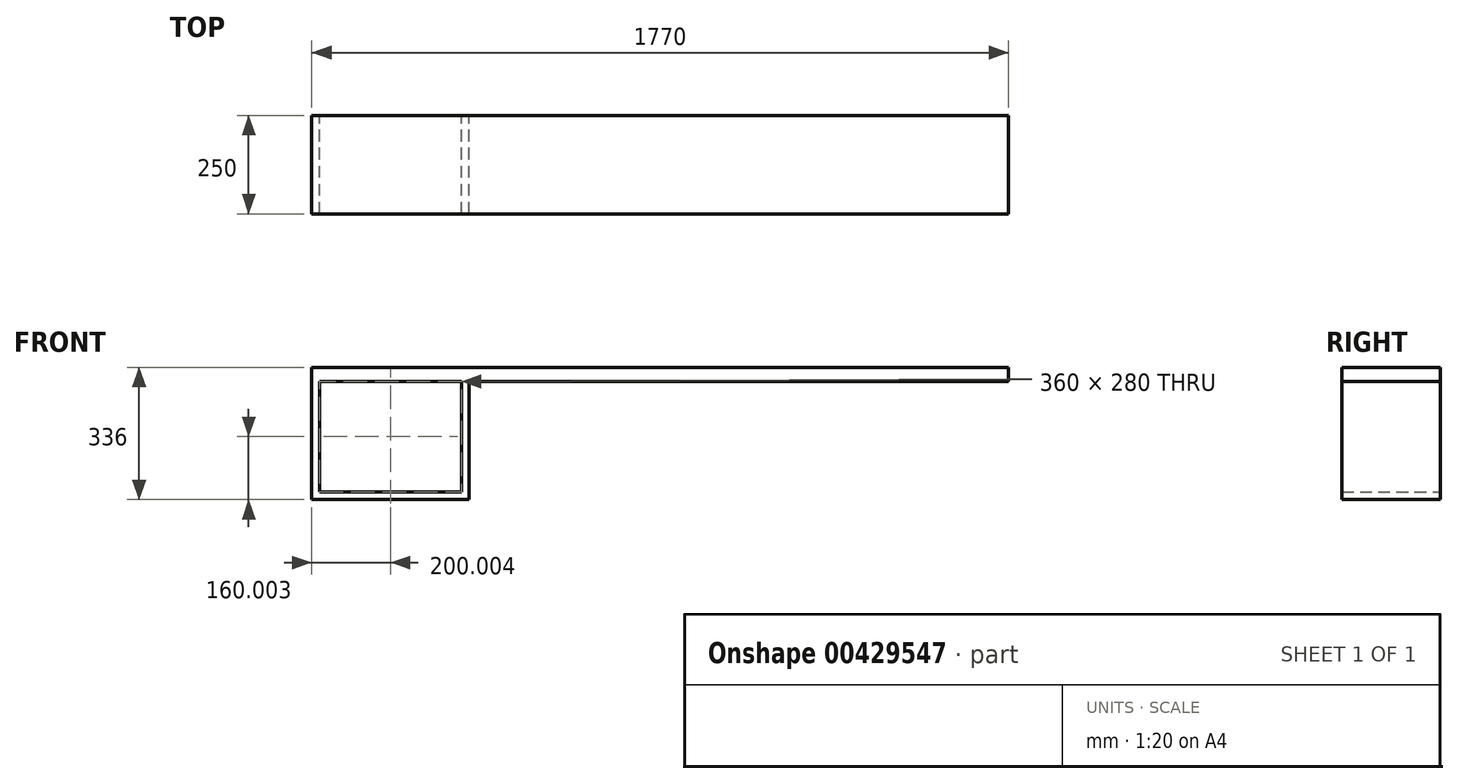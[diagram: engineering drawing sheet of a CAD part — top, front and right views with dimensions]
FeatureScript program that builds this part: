
annotation { "Feature Type Name" : "Feature", "Feature Type Description" : "" }
export const myFeature = defineFeature(function(context is Context, id is Id, definition is map)
    precondition{}
    {
        {
            var Q0;
            Q0=qCreatedBy(makeId("Front.planeOp"),FACE);
            var sketch = newSketch(context, id + "F0", { "sketchPlane" : qUnion([Q0])});
            skLineSegment(sketch, "E0.top", {"start": v(1486.02, 125.11) * mm, "end": v(-283.98, 125.11) * mm});
            skLineSegment(sketch, "E0.left", {"start": v(1486.02, 89.11) * mm, "end": v(1486.02, 125.11) * mm});
            skLineSegment(sketch, "E0.right", {"start": v(-283.98, -60.89) * mm, "end": v(-283.98, 125.11) * mm});
            skPoint(sketch, "E0.middle", {"position": v(601.02, 0.11) * mm});
            skLineSegment(sketch, "E1.0", {"start": v(1486.02, 89.11) * mm, "end": v(-283.98, 89.11) * mm});
            skLineSegment(sketch, "E2.0", {"start": v(116.02, -60.89) * mm, "end": v(116.02, 125.11) * mm});
            skLineSegment(sketch, "E3.0", {"start": v(116.02, -60.89) * mm, "end": v(-283.98, -60.89) * mm});
            skLineSegment(sketch, "E4.0", {"start": v(116.02, -210.89) * mm, "end": v(-283.98, -210.89) * mm});
            skPoint(sketch, "E5.orphan", {"position": v(1486.02, -124.89) * mm});
            skPoint(sketch, "E6.orphan", {"position": v(-283.98, -124.89) * mm});
            skLineSegment(sketch, "E7", {"start": v(116.02, -60.89) * mm, "end": v(116.02, -210.89) * mm});
            skLineSegment(sketch, "E8", {"start": v(-283.98, -60.89) * mm, "end": v(-283.98, -210.89) * mm});
            skLineSegment(sketch, "E9.0", {"start": v(96.02, -60.89) * mm, "end": v(96.02, 125.11) * mm});
            skLineSegment(sketch, "E9.1", {"start": v(96.02, -60.89) * mm, "end": v(96.02, -210.89) * mm});
            skLineSegment(sketch, "E10.0", {"start": v(116.02, -190.89) * mm, "end": v(-283.98, -190.89) * mm});
            skLineSegment(sketch, "E11.0", {"start": v(-263.98, -60.89) * mm, "end": v(-263.98, -210.89) * mm});
            skLineSegment(sketch, "E12.0", {"start": v(-263.98, -60.89) * mm, "end": v(-263.98, 125.11) * mm});
            skSolve(sketch);
        }
        {
            var Q0;
            {var subQ0=sQuery(id+"F0.wireOp",EDGE,"E0.left");Q0=makeQuery(id+"F0.imprint","IMPRINT",FACE,{"disambiguationData":[TD([[makeQuery(id+"F0.imprint","IMPRINT",EDGE,{"derivedFrom":subQ0}),1.0]])]});}
            var Q1;
            {var subQ0=sQuery(id+"F0.wireOp",EDGE,"E0.right");var subQ1=sQuery(id+"F0.wireOp",EDGE,"E0.top");var subQ2=makeQuery(id+"F0.imprint","INTERSECT",VERTEX,{"derivedFrom":[subQ1,subQ0]});Q1=makeQuery(id+"F0.imprint","IMPRINT",FACE,{"disambiguationData":[TD([[makeQuery(id+"F0.imprint","IMPRINT",EDGE,{"disambiguationData":[TD([[subQ2,1.0]])],"derivedFrom":subQ1}),1.0]])]});}
            var Q2;
            {var subQ0=sQuery(id+"F0.wireOp",EDGE,"E9.0");var subQ1=sQuery(id+"F0.wireOp",EDGE,"E0.top");var subQ2=makeQuery(id+"F0.imprint","INTERSECT",VERTEX,{"derivedFrom":[subQ1,subQ0]});Q2=makeQuery(id+"F0.imprint","IMPRINT",FACE,{"disambiguationData":[TD([[makeQuery(id+"F0.imprint","IMPRINT",EDGE,{"disambiguationData":[TD([[subQ2,-1.0]])],"derivedFrom":subQ1}),1.0]])]});}
            var Q3;
            {var subQ0=sQuery(id+"F0.wireOp",EDGE,"E2.0");var subQ1=sQuery(id+"F0.wireOp",EDGE,"E0.top");var subQ2=makeQuery(id+"F0.imprint","INTERSECT",VERTEX,{"derivedFrom":[subQ1,subQ0]});Q3=makeQuery(id+"F0.imprint","IMPRINT",FACE,{"disambiguationData":[TD([[makeQuery(id+"F0.imprint","IMPRINT",EDGE,{"disambiguationData":[TD([[subQ2,-1.0]])],"derivedFrom":subQ1}),1.0]])]});}
            extrude(context, id + "F1", {"entities" : qUnion([Q0, Q1, Q2, Q3]), "depth" : 250 * mm});
        }
        {
            var Q0;
            {var subQ1=sQuery(id+"F0.wireOp",EDGE,"E0.right");var subQ3=sQuery(id+"F0.wireOp",EDGE,"E1.0");var subQ4=makeQuery(id+"F0.imprint","INTERSECT",VERTEX,{"derivedFrom":[subQ1,subQ3]});Q0=makeQuery(id+"F0.imprint","IMPRINT",FACE,{"disambiguationData":[TD([[makeQuery(id+"F0.imprint","IMPRINT",EDGE,{"disambiguationData":[TD([[subQ4,1.0]])],"derivedFrom":subQ3}),1.0]])]});}
            var Q1;
            {var subQ0=sQuery(id+"F0.wireOp",EDGE,"E8");var subQ5=sQuery(id+"F0.wireOp",EDGE,"E10.0");var subQ7=makeQuery(id+"F0.imprint","INTERSECT",VERTEX,{"derivedFrom":[subQ0,subQ5]});Q1=makeQuery(id+"F0.imprint","IMPRINT",FACE,{"disambiguationData":[TD([[makeQuery(id+"F0.imprint","IMPRINT",EDGE,{"disambiguationData":[TD([[subQ7,1.0]])],"derivedFrom":subQ5}),-1.0]])]});}
            var Q2;
            {var subQ0=sQuery(id+"F0.wireOp",EDGE,"E8");var subQ1=sQuery(id+"F0.wireOp",EDGE,"E4.0");var subQ2=makeQuery(id+"F0.imprint","INTERSECT",VERTEX,{"derivedFrom":[subQ1,subQ0]});Q2=makeQuery(id+"F0.imprint","IMPRINT",FACE,{"disambiguationData":[TD([[makeQuery(id+"F0.imprint","IMPRINT",EDGE,{"disambiguationData":[TD([[subQ2,1.0]])],"derivedFrom":subQ1}),-1.0]])]});}
            var Q3;
            {var subQ0=sQuery(id+"F0.wireOp",EDGE,"E9.1");var subQ1=sQuery(id+"F0.wireOp",EDGE,"E4.0");var subQ2=makeQuery(id+"F0.imprint","INTERSECT",VERTEX,{"derivedFrom":[subQ1,subQ0]});Q3=makeQuery(id+"F0.imprint","IMPRINT",FACE,{"disambiguationData":[TD([[makeQuery(id+"F0.imprint","IMPRINT",EDGE,{"disambiguationData":[TD([[subQ2,-1.0]])],"derivedFrom":subQ1}),-1.0]])]});}
            var Q4;
            {var subQ0=sQuery(id+"F0.wireOp",EDGE,"E7");var subQ1=sQuery(id+"F0.wireOp",EDGE,"E4.0");var subQ2=makeQuery(id+"F0.imprint","INTERSECT",VERTEX,{"derivedFrom":[subQ1,subQ0]});Q4=makeQuery(id+"F0.imprint","IMPRINT",FACE,{"disambiguationData":[TD([[makeQuery(id+"F0.imprint","IMPRINT",EDGE,{"disambiguationData":[TD([[subQ2,-1.0]])],"derivedFrom":subQ1}),-1.0]])]});}
            var Q5;
            {var subQ0=sQuery(id+"F0.wireOp",EDGE,"E7");var subQ5=sQuery(id+"F0.wireOp",EDGE,"E10.0");var subQ6=makeQuery(id+"F0.imprint","INTERSECT",VERTEX,{"derivedFrom":[subQ0,subQ5]});Q5=makeQuery(id+"F0.imprint","IMPRINT",FACE,{"disambiguationData":[TD([[makeQuery(id+"F0.imprint","IMPRINT",EDGE,{"disambiguationData":[TD([[subQ6,-1.0]])],"derivedFrom":subQ5}),-1.0]])]});}
            var Q6;
            {var subQ0=sQuery(id+"F0.wireOp",EDGE,"E2.0");var subQ1=sQuery(id+"F0.wireOp",EDGE,"E1.0");var subQ2=makeQuery(id+"F0.imprint","INTERSECT",VERTEX,{"derivedFrom":[subQ1,subQ0]});Q6=makeQuery(id+"F0.imprint","IMPRINT",FACE,{"disambiguationData":[TD([[makeQuery(id+"F0.imprint","IMPRINT",EDGE,{"disambiguationData":[TD([[subQ2,-1.0]])],"derivedFrom":subQ1}),1.0]])]});}
            extrude(context, id + "F2", {"entities" : qUnion([Q0, Q1, Q2, Q3, Q4, Q5, Q6]), "operationType" : NewBodyOperationType.ADD, "depth" : 250 * mm});
        }
    });
